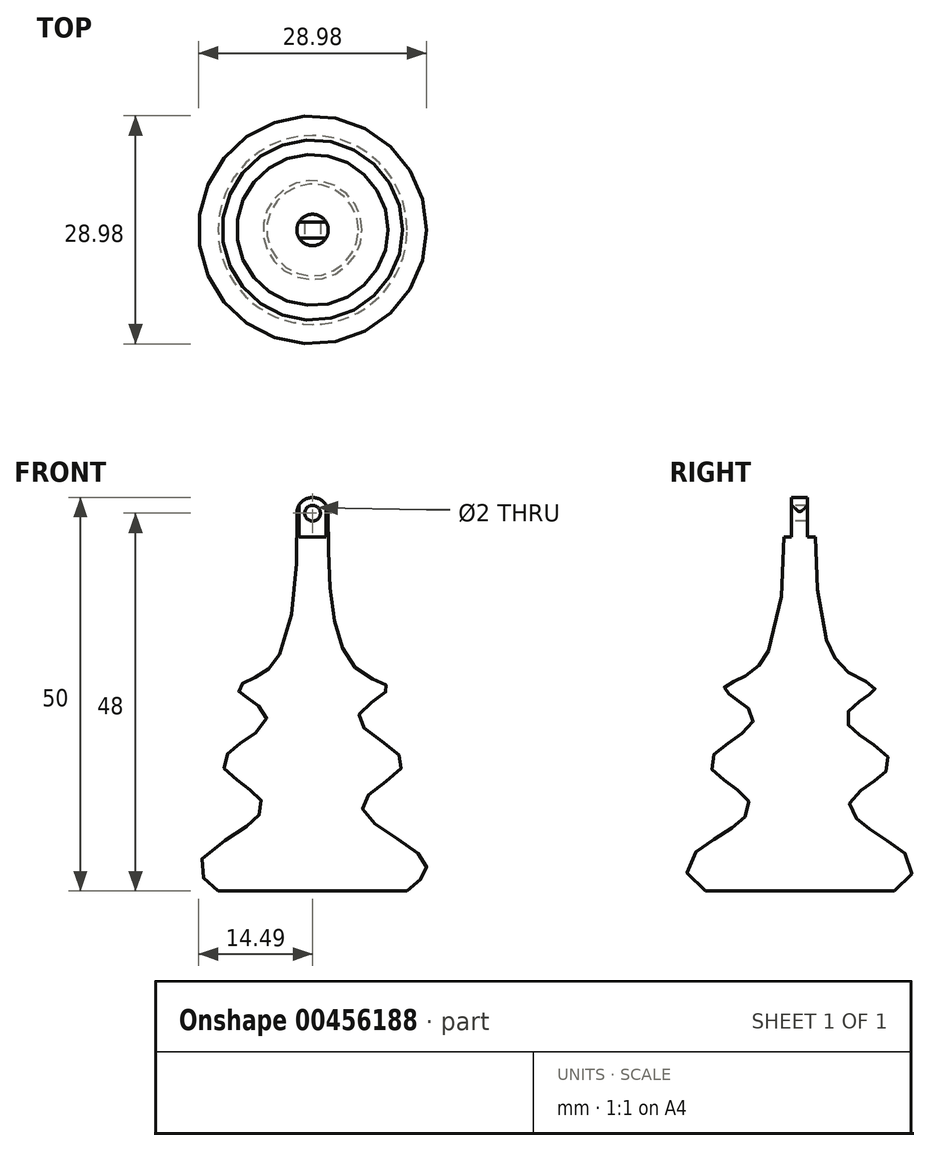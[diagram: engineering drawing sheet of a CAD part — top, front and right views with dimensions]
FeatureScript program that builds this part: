
annotation { "Feature Type Name" : "Feature", "Feature Type Description" : "" }
export const myFeature = defineFeature(function(context is Context, id is Id, definition is map)
    precondition{}
    {
        {
            var Q0;
            Q0=qCreatedBy(makeId("Front.planeOp"),FACE);
            var sketch = newSketch(context, id + "F0", { "sketchPlane" : qUnion([Q0])});
            skLineSegment(sketch, "E0", {"start": v(0, 66.42) * mm, "end": v(0, -45.62) * mm, "construction": true});
            skLineSegment(sketch, "E1", {"start": v(0, 0) * mm, "end": v(12, 0) * mm});
            skLineSegment(sketch, "E2", {"start": v(0, 0) * mm, "end": v(0, 50) * mm});
            skLineSegment(sketch, "E3", {"start": v(0, 50) * mm, "end": v(2, 50) * mm});
            skFitSpline(sketch, "E4", {"points": [v(2, 50) * mm, v(5.64, 28.19) * mm, v(9.58, 25.66) * mm, v(5.83, 21.9) * mm, v(11.45, 16.29) * mm, v(6.3, 10.85) * mm, v(14.26, 3.83) * mm, v(12, 0) * mm], "startDerivative": vector(-0.6, -118.75) * mm, "endDerivative": vector(-43.91, -34.76) * mm});
            skSolve(sketch);
        }
        {
            var Q0;
            Q0=makeQuery(id+"F0.imprint","IMPRINT",FACE,{"disambiguationData":[TD([[makeQuery(id+"F0.imprint","IMPRINT",EDGE,{"derivedFrom":sQuery(id+"F0.wireOp",EDGE,"E1")}),1.0]])]});
            var Q1;
            Q1=sQuery(id+"F0.wireOp",EDGE,"E0");
            revolve(context, id + "F1", {"entities" : qUnion([Q0]), "axis" : qUnion([Q1]), "revolveType" : RevolveType.FULL});
        }
        {
            var Q0;
            Q0=makeQuery(id+"F1.opRevolve","SWEPT_FACE",FACE,{"disambiguationData":[OSD([sQuery(id+"F0.wireOp",EDGE,"E3")])]});
            var sketch = newSketch(context, id + "F2", { "sketchPlane" : qUnion([Q0])});
            skLineSegment(sketch, "E5.bottom", {"start": v(-3.07, -1.02) * mm, "end": v(2.93, -1.02) * mm});
            skLineSegment(sketch, "E5.top", {"start": v(-3.07, 0.98) * mm, "end": v(2.93, 0.98) * mm});
            skLineSegment(sketch, "E5.left", {"start": v(-3.07, -1.02) * mm, "end": v(-3.07, 0.98) * mm});
            skLineSegment(sketch, "E5.right", {"start": v(2.93, -1.02) * mm, "end": v(2.93, 0.98) * mm});
            skSolve(sketch);
        }
        {
            var Q0;
            {var subQ0=sQuery(id+"F2.wireOp",EDGE,"E5.top");var subQ1=makeQuery(id+"F1.opRevolve","SWEPT_EDGE",EDGE,{"disambiguationData":[OSD([sQuery(id+"F0.wireOp",EDGE,"E3"),sQuery(id+"F0.wireOp",EDGE,"E4")])]});var subQ2=makeQuery(id+"F2.imprint","INTERSECT",VERTEX,{"disambiguationData":[OD(0.0)],"derivedFrom":[subQ1,subQ0]});Q0=makeQuery(id+"F2.imprint","IMPRINT",FACE,{"disambiguationData":[TD([[makeQuery(id+"F2.imprint","IMPRINT",EDGE,{"disambiguationData":[TD([[subQ2,-1.0]])],"derivedFrom":subQ0}),1.0]])]});}
            var Q1;
            {var subQ0=sQuery(id+"F2.wireOp",EDGE,"E5.bottom");var subQ1=makeQuery(id+"F1.opRevolve","SWEPT_EDGE",EDGE,{"disambiguationData":[OSD([sQuery(id+"F0.wireOp",EDGE,"E3"),sQuery(id+"F0.wireOp",EDGE,"E4")])]});var subQ2=makeQuery(id+"F2.imprint","INTERSECT",VERTEX,{"disambiguationData":[OD(0.0)],"derivedFrom":[subQ1,subQ0]});Q1=makeQuery(id+"F2.imprint","IMPRINT",FACE,{"disambiguationData":[TD([[makeQuery(id+"F2.imprint","IMPRINT",EDGE,{"disambiguationData":[TD([[subQ2,-1.0]])],"derivedFrom":subQ0}),-1.0]])]});}
            extrude(context, id + "F3", {"entities" : qUnion([Q0, Q1]), "operationType" : NewBodyOperationType.REMOVE, "oppositeDirection" : true, "depth" : 5 * mm});
        }
        {
            var Q0;
            Q0=qCreatedBy(makeId("Front.planeOp"),FACE);
            var sketch = newSketch(context, id + "F4", { "sketchPlane" : qUnion([Q0])});
            skArc(sketch, "E6", {"start": v(2, 48) * mm, "mid": v(0, 50) * mm, "end": v(-2, 48) * mm});
            skLineSegment(sketch, "E7", {"start": v(2, 48) * mm, "end": v(2, 50.5) * mm});
            skLineSegment(sketch, "E8", {"start": v(2, 50.5) * mm, "end": v(-2, 50.5) * mm});
            skLineSegment(sketch, "E9", {"start": v(-2, 50.5) * mm, "end": v(-2, 48) * mm});
            skSolve(sketch);
        }
        {
            var Q0;
            {var subQ0=sQuery(id+"F4.wireOp",EDGE,"E6");Q0=makeQuery(id+"F4.imprint","IMPRINT",FACE,{"disambiguationData":[TD([[makeQuery(id+"F4.imprint","IMPRINT",EDGE,{"derivedFrom":subQ0}),-1.0]])]});}
            extrude(context, id + "F5", {"entities" : qUnion([Q0]), "operationType" : NewBodyOperationType.REMOVE, "endBound" : BoundingType.SYMMETRIC, "depth" : 5 * mm});
        }
        {
            var Q0;
            Q0=qCreatedBy(makeId("Front.planeOp"),FACE);
            var sketch = newSketch(context, id + "F6", { "sketchPlane" : qUnion([Q0])});
            skCircle(sketch, "E10", {"center": v(0, 48) * mm, "radius": 1 * mm});
            skSolve(sketch);
        }
        {
            var Q0;
            Q0 = qSketchRegion(id + "F6", true);
            extrude(context, id + "F7", {"entities" : qUnion([Q0]), "operationType" : NewBodyOperationType.REMOVE, "endBound" : BoundingType.SYMMETRIC, "oppositeDirection" : true, "depth" : 4 * mm});
        }
    });
